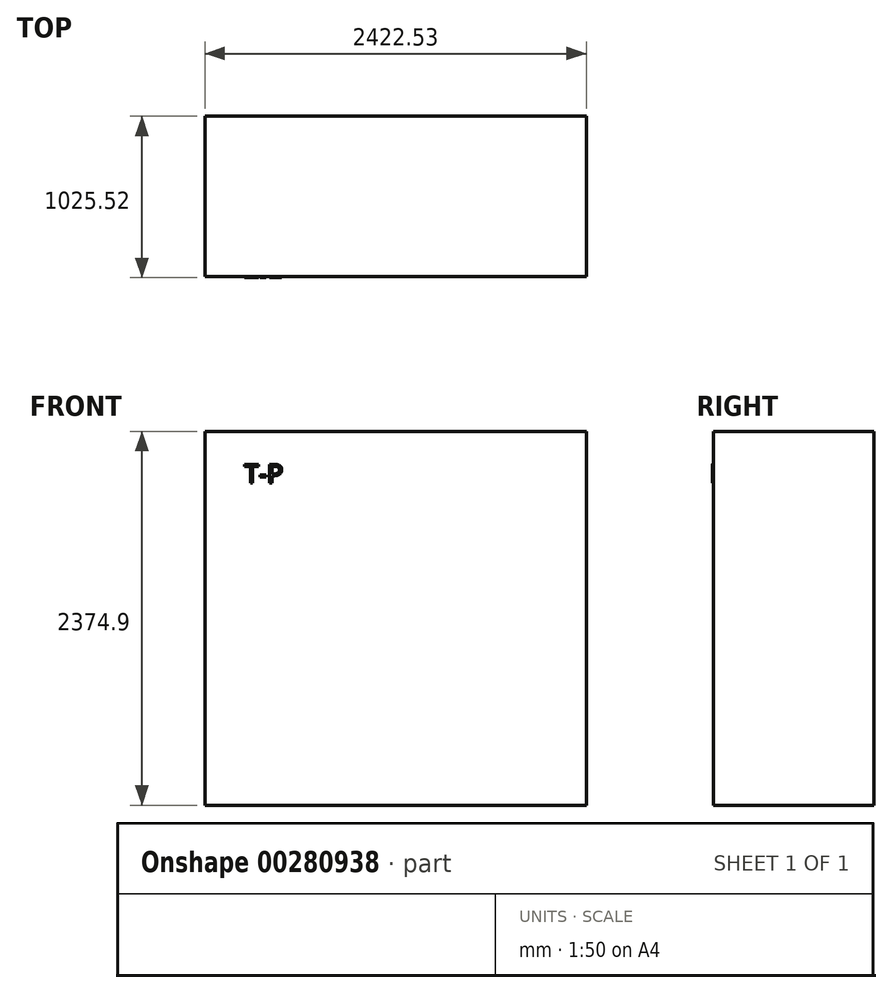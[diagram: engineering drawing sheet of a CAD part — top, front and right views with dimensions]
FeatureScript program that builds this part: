
annotation { "Feature Type Name" : "Feature", "Feature Type Description" : "" }
export const myFeature = defineFeature(function(context is Context, id is Id, definition is map)
    precondition{}
    {
        {
            var Q0;
            Q0=qCreatedBy(makeId("Top.planeOp"),FACE);
            var sketch = newSketch(context, id + "F0", { "sketchPlane" : qUnion([Q0])});
            skLineSegment(sketch, "E0.bottom", {"start": v(0, 0) * mm, "end": v(2422.53, 0) * mm});
            skLineSegment(sketch, "E0.top", {"start": v(0, 1019.18) * mm, "end": v(2422.53, 1019.18) * mm});
            skLineSegment(sketch, "E0.left", {"start": v(0, 0) * mm, "end": v(0, 1019.18) * mm});
            skLineSegment(sketch, "E0.right", {"start": v(2422.53, 0) * mm, "end": v(2422.53, 1019.18) * mm});
            skSolve(sketch);
        }
        {
            var Q0;
            Q0=makeQuery(id+"F0.imprint","IMPRINT",FACE,{"disambiguationData":[TD([[makeQuery(id+"F0.imprint","IMPRINT",EDGE,{"derivedFrom":sQuery(id+"F0.wireOp",EDGE,"E0.bottom")}),1.0]])]});
            extrude(context, id + "F1", {"entities" : qUnion([Q0]), "depth" : 2374.9 * mm});
        }
        {
            var Q0;
            Q0=makeQuery(id+"F1.opExtrude","SWEPT_FACE",FACE,{"disambiguationData":[OSD([sQuery(id+"F0.wireOp",EDGE,"E0.bottom")])]});
            var sketch = newSketch(context, id + "F2", { "sketchPlane" : qUnion([Q0])});
            skText(sketch, "E1", { "text": "T-P", "fontName": "OpenSans-Regular.ttf"});
            const initialGuessF2  = {"E1": [0.24958, 2.04556, 1, 0, 0.12011]};
            skSetInitialGuess(sketch, initialGuessF2);
            skSolve(sketch);
        }
        {
            var Q0;
            Q0 = qSketchRegion(id + "F2", true);
            extrude(context, id + "F3", {"entities" : qUnion([Q0]), "operationType" : NewBodyOperationType.ADD, "depth" : 6.35 * mm});
        }
    });
